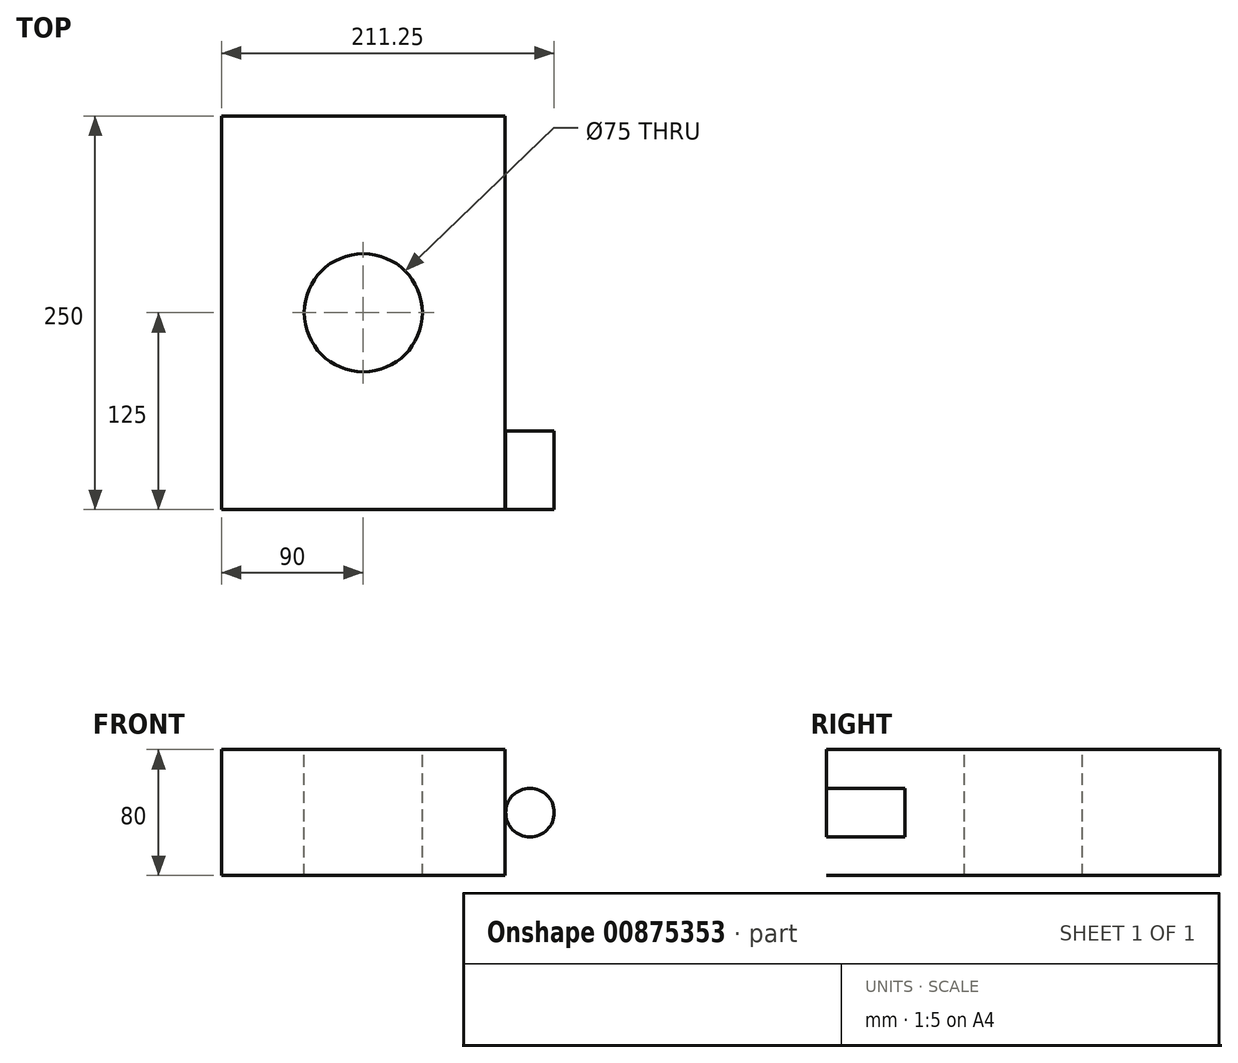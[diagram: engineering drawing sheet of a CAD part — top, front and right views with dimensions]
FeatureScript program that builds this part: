
annotation { "Feature Type Name" : "Feature", "Feature Type Description" : "" }
export const myFeature = defineFeature(function(context is Context, id is Id, definition is map)
    precondition{}
    {
        {
            var Q0;
            Q0=qCreatedBy(makeId("Front.planeOp"),FACE);
            var sketch = newSketch(context, id + "F0", { "sketchPlane" : qUnion([Q0])});
            skLineSegment(sketch, "E0.bottom", {"start": v(90, 40) * mm, "end": v(-90, 40) * mm});
            skLineSegment(sketch, "E0.top", {"start": v(90, -40) * mm, "end": v(-90, -40) * mm});
            skLineSegment(sketch, "E0.left", {"start": v(90, 40) * mm, "end": v(90, -40) * mm});
            skLineSegment(sketch, "E0.right", {"start": v(-90, 40) * mm, "end": v(-90, -40) * mm});
            skPoint(sketch, "E0.middle", {"position": v(0, 0) * mm});
            skSolve(sketch);
        }
        {
            var Q0;
            Q0=makeQuery(id+"F0.imprint","IMPRINT",FACE,{"disambiguationData":[TD([[makeQuery(id+"F0.imprint","IMPRINT",EDGE,{"derivedFrom":sQuery(id+"F0.wireOp",EDGE,"E0.bottom")}),1.0]])]});
            extrude(context, id + "F1", {"entities" : qUnion([Q0]), "endBound" : BoundingType.SYMMETRIC, "depth" : 250 * mm, "offsetDistance" : 25 * mm});
        }
        {
            var Q0;
            Q0=makeQuery(id+"F1.opExtrude","SWEPT_FACE",FACE,{"disambiguationData":[OSD([sQuery(id+"F0.wireOp",EDGE,"E0.bottom")])]});
            var sketch = newSketch(context, id + "F2", { "sketchPlane" : qUnion([Q0])});
            skCircle(sketch, "E1", {"center": v(0, 0) * mm, "radius": 37.5 * mm});
            skSolve(sketch);
        }
        {
            var Q0;
            Q0=makeQuery(id+"F2.imprint","IMPRINT",FACE,{"disambiguationData":[TD([[makeQuery(id+"F2.imprint","IMPRINT",EDGE,{"derivedFrom":sQuery(id+"F2.wireOp",EDGE,"E1")}),1.0]])]});
            extrude(context, id + "F3", {"entities" : qUnion([Q0]), "operationType" : NewBodyOperationType.REMOVE, "oppositeDirection" : true, "depth" : 100 * mm, "offsetDistance" : 25 * mm});
        }
        {
            var Q0;
            Q0=qCreatedBy(makeId("Front.planeOp"),FACE);
            cPlane(context, id + "F4", {"entities" : qUnion([Q0]), "cplaneType" : CPlaneType.OFFSET, "offset" : 125 * mm, "width" : 150 * mm, "height" : 150 * mm});
        }
        {
            var Q0;
            Q0=qCreatedBy(id+"F4.planeOp",FACE);
            var sketch = newSketch(context, id + "F5", { "sketchPlane" : qUnion([Q0])});
            skCircle(sketch, "E2", {"center": v(105.83, 0) * mm, "radius": 15.42 * mm});
            skSolve(sketch);
        }
        {
            var Q0;
            Q0 = qSketchRegion(id + "F5", true);
            extrude(context, id + "F6", {"entities" : qUnion([Q0]), "oppositeDirection" : true, "depth" : 50 * mm, "offsetDistance" : 25 * mm});
        }
    });
